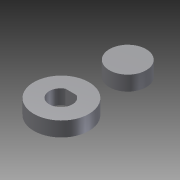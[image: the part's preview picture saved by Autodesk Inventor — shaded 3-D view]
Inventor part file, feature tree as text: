
AUTODESK INVENTOR PART (.ipt)
format: ipt  version: 2012 (Build 160160000, 160)  size: 83,968 bytes
history: native  units: mm
features: reference x2, extrude x1, sketch x1
ambient origin geometry x8: Origin, YZ Plane, XZ Plane, XY Plane, X Axis, Y Axis, Z Axis, Center Point
bodies: Solid1 (feature_tree)
feature tree (4):
  extrude  "Extrusion1"  Depth=6.0mm
  sketch  "Sketch1"  dims[d0=0.3mm d1=6.0mm d2=6.3mm d3=15.0mm d4=10.0mm d5=4.0mm d6=0.0mm]
  reference  "Reference1"
  reference  "Reference2"
